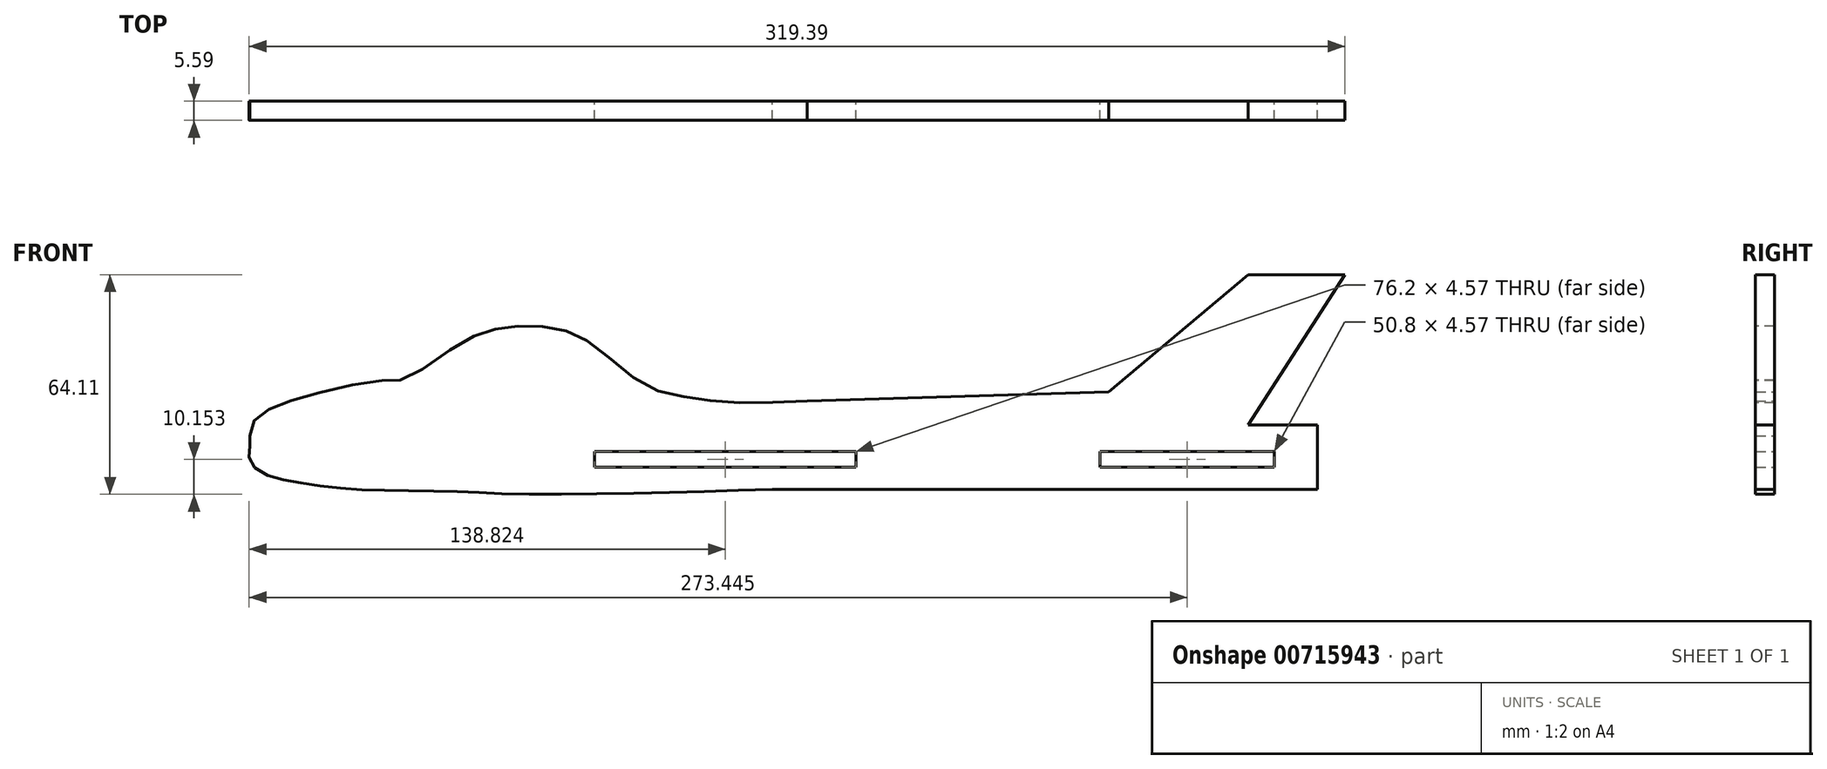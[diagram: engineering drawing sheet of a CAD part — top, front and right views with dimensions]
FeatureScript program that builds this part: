
annotation { "Feature Type Name" : "Feature", "Feature Type Description" : "" }
export const myFeature = defineFeature(function(context is Context, id is Id, definition is map)
    precondition{}
    {
        {
            var Q0;
            Q0=qCreatedBy(makeId("Front.planeOp"),FACE);
            var sketch = newSketch(context, id + "F0", { "sketchPlane" : qUnion([Q0])});
            skLineSegment(sketch, "E0.bottom", {"start": v(0, 0) * mm, "end": v(381, 0) * mm});
            skLineSegment(sketch, "E0.top", {"start": v(0, 101.6) * mm, "end": v(381, 101.6) * mm});
            skLineSegment(sketch, "E0.left", {"start": v(0, 0) * mm, "end": v(0, 101.6) * mm});
            skLineSegment(sketch, "E0.right", {"start": v(381, 0) * mm, "end": v(381, 101.6) * mm});
            skFitSpline(sketch, "E1", {"points": [v(5.18, 34.12) * mm, v(6.4, 38.58) * mm, v(12.5, 42.64) * mm, v(25.48, 46.7) * mm, v(44.16, 50.36) * mm, v(50.25, 50.76) * mm, v(64.87, 60.1) * mm, v(75.43, 64.98) * mm, v(85.17, 66.2) * mm, v(96.54, 64.98) * mm, v(105.47, 60.5) * mm, v(119.28, 49.55) * mm, v(131.86, 45.49) * mm, v(146.48, 43.86) * mm, v(167.6, 44.27) * mm], "startDerivative": vector(10.59, 107.02) * mm, "endDerivative": vector(234.4, 10.65) * mm});
            skFitSpline(sketch, "E2", {"points": [v(5.18, 34.12) * mm, v(5.18, 30.86) * mm, v(5.18, 26.83) * mm, v(9.75, 22.85) * mm, v(18.38, 20.66) * mm, v(30.66, 18.98) * mm, v(46.17, 18.2) * mm, v(65.33, 17.94) * mm, v(82.06, 17.2) * mm, v(119.13, 17.45) * mm, v(157.39, 18.55) * mm], "startDerivative": vector(3.73, -65.2) * mm, "endDerivative": vector(225.88, 7.23) * mm});
            skLineSegment(sketch, "E3", {"start": v(157.39, 18.55) * mm, "end": v(316.28, 18.55) * mm});
            skLineSegment(sketch, "E4", {"start": v(316.28, 18.55) * mm, "end": v(316.28, 37.38) * mm});
            skLineSegment(sketch, "E5", {"start": v(316.28, 37.38) * mm, "end": v(296.14, 37.38) * mm});
            skLineSegment(sketch, "E6", {"start": v(296.14, 37.38) * mm, "end": v(324.32, 81.2) * mm});
            skLineSegment(sketch, "E7", {"start": v(324.32, 81.2) * mm, "end": v(296.14, 81.2) * mm});
            skLineSegment(sketch, "E8", {"start": v(296.14, 81.2) * mm, "end": v(255.42, 47.03) * mm});
            skLineSegment(sketch, "E9", {"start": v(255.42, 47.03) * mm, "end": v(167.6, 44.27) * mm});
            skLineSegment(sketch, "E10.bottom", {"start": v(105.65, 29.52) * mm, "end": v(181.85, 29.52) * mm});
            skLineSegment(sketch, "E10.top", {"start": v(105.65, 24.95) * mm, "end": v(181.85, 24.95) * mm});
            skLineSegment(sketch, "E10.left", {"start": v(105.65, 29.52) * mm, "end": v(105.65, 24.95) * mm});
            skLineSegment(sketch, "E10.right", {"start": v(181.85, 29.52) * mm, "end": v(181.85, 24.95) * mm});
            skLineSegment(sketch, "E11.bottom", {"start": v(252.97, 24.95) * mm, "end": v(303.77, 24.95) * mm});
            skLineSegment(sketch, "E11.top", {"start": v(252.97, 29.52) * mm, "end": v(303.77, 29.52) * mm});
            skLineSegment(sketch, "E11.left", {"start": v(252.97, 24.95) * mm, "end": v(252.97, 29.52) * mm});
            skLineSegment(sketch, "E11.right", {"start": v(303.77, 24.95) * mm, "end": v(303.77, 29.52) * mm});
            skSolve(sketch);
        }
        {
            var Q0;
            Q0=makeQuery(id+"F0.imprint","IMPRINT",FACE,{"disambiguationData":[TD([[makeQuery(id+"F0.imprint","IMPRINT",EDGE,{"derivedFrom":sQuery(id+"F0.wireOp",EDGE,"E1")}),-1.0]])]});
            extrude(context, id + "F1", {"entities" : qUnion([Q0]), "depth" : 5.6 * mm, "offsetDistance" : 25.4 * mm});
        }
    });
